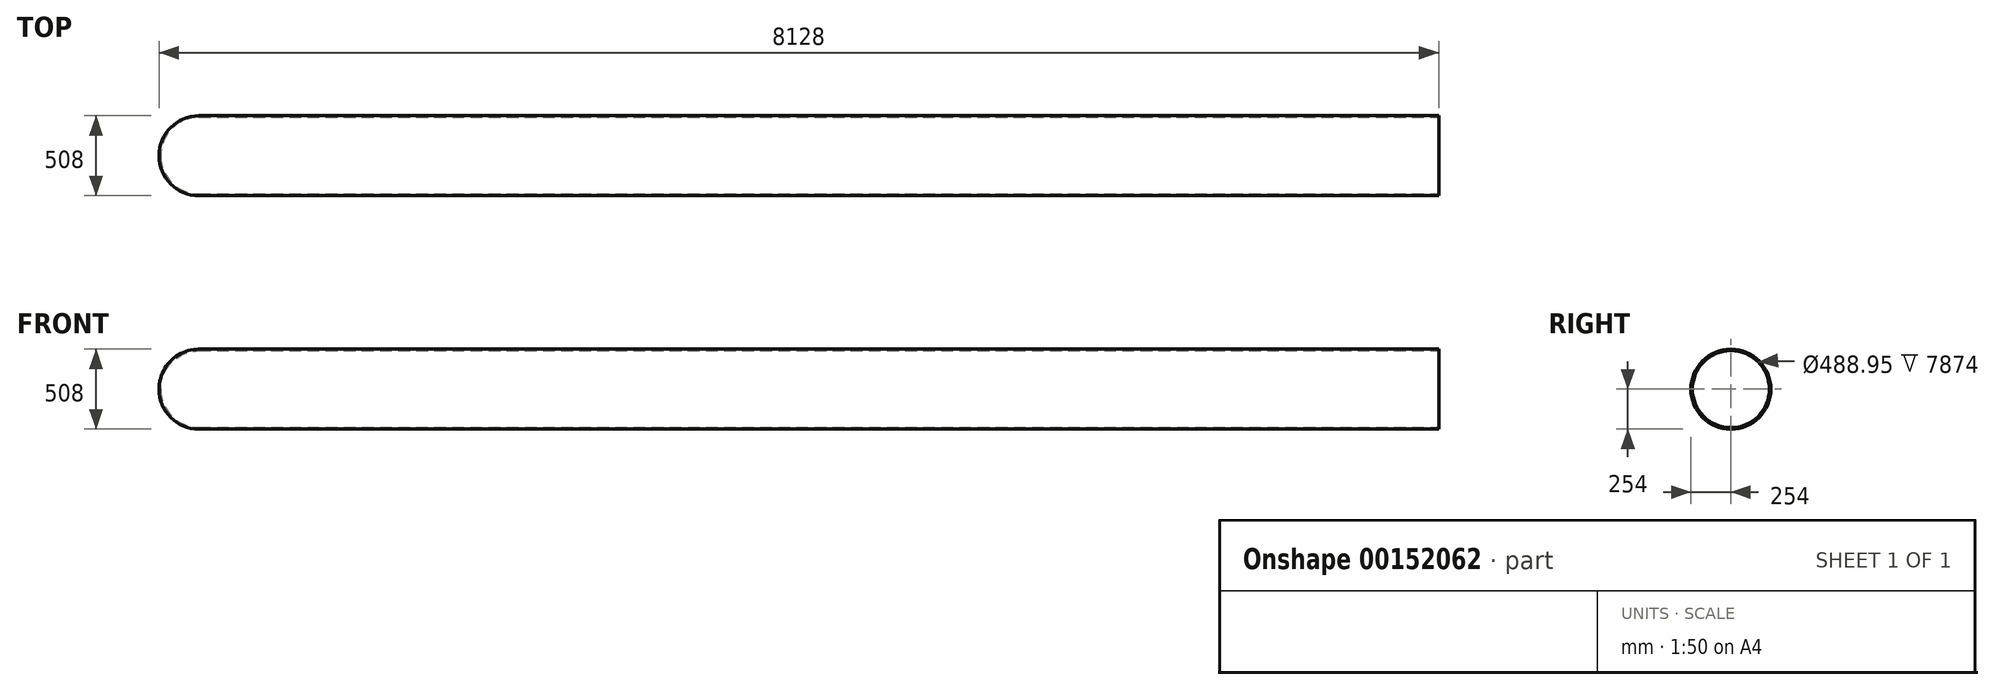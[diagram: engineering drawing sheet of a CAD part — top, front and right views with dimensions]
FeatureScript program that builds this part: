
annotation { "Feature Type Name" : "Feature", "Feature Type Description" : "" }
export const myFeature = defineFeature(function(context is Context, id is Id, definition is map)
    precondition{}
    {
        {
            var Q0;
            Q0=qCreatedBy(makeId("Front.planeOp"),FACE);
            var sketch = newSketch(context, id + "F0", { "sketchPlane" : qUnion([Q0])});
            skLineSegment(sketch, "E0.bottom", {"start": v(3937, 127) * mm, "end": v(-3937, 127) * mm});
            skLineSegment(sketch, "E0.top", {"start": v(3937, -127) * mm, "end": v(-3937, -127) * mm});
            skLineSegment(sketch, "E0.left", {"start": v(3937, 127) * mm, "end": v(3937, -127) * mm});
            skLineSegment(sketch, "E0.right", {"start": v(-3937, 127) * mm, "end": v(-3937, -127) * mm});
            skPoint(sketch, "E0.middle", {"position": v(0, 0) * mm});
            skArc(sketch, "E1", {"start": v(-3937, 127) * mm, "mid": v(-4116.6, 52.6) * mm, "end": v(-4191, -127) * mm});
            skLineSegment(sketch, "E2", {"start": v(-3937, -127) * mm, "end": v(-4191, -127) * mm});
            skSolve(sketch);
        }
        {
            var Q0;
            Q0 = qSketchRegion(id + "F0", true);
            var Q1;
            Q1=sQuery(id+"F0.wireOp",EDGE,"E0.top");
            revolve(context, id + "F1", {"entities" : qUnion([Q0]), "axis" : qUnion([Q1]), "revolveType" : RevolveType.FULL});
        }
        {
            var Q0;
            Q0=makeQuery(id+"F1.opRevolve","SWEPT_FACE",FACE,{"disambiguationData":[OSD([sQuery(id+"F0.wireOp",EDGE,"E0.left")])]});
            shell(context, id + "F2", {"entities" : qUnion([Q0]), "thickness" : 9.52 * mm});
        }
    });
